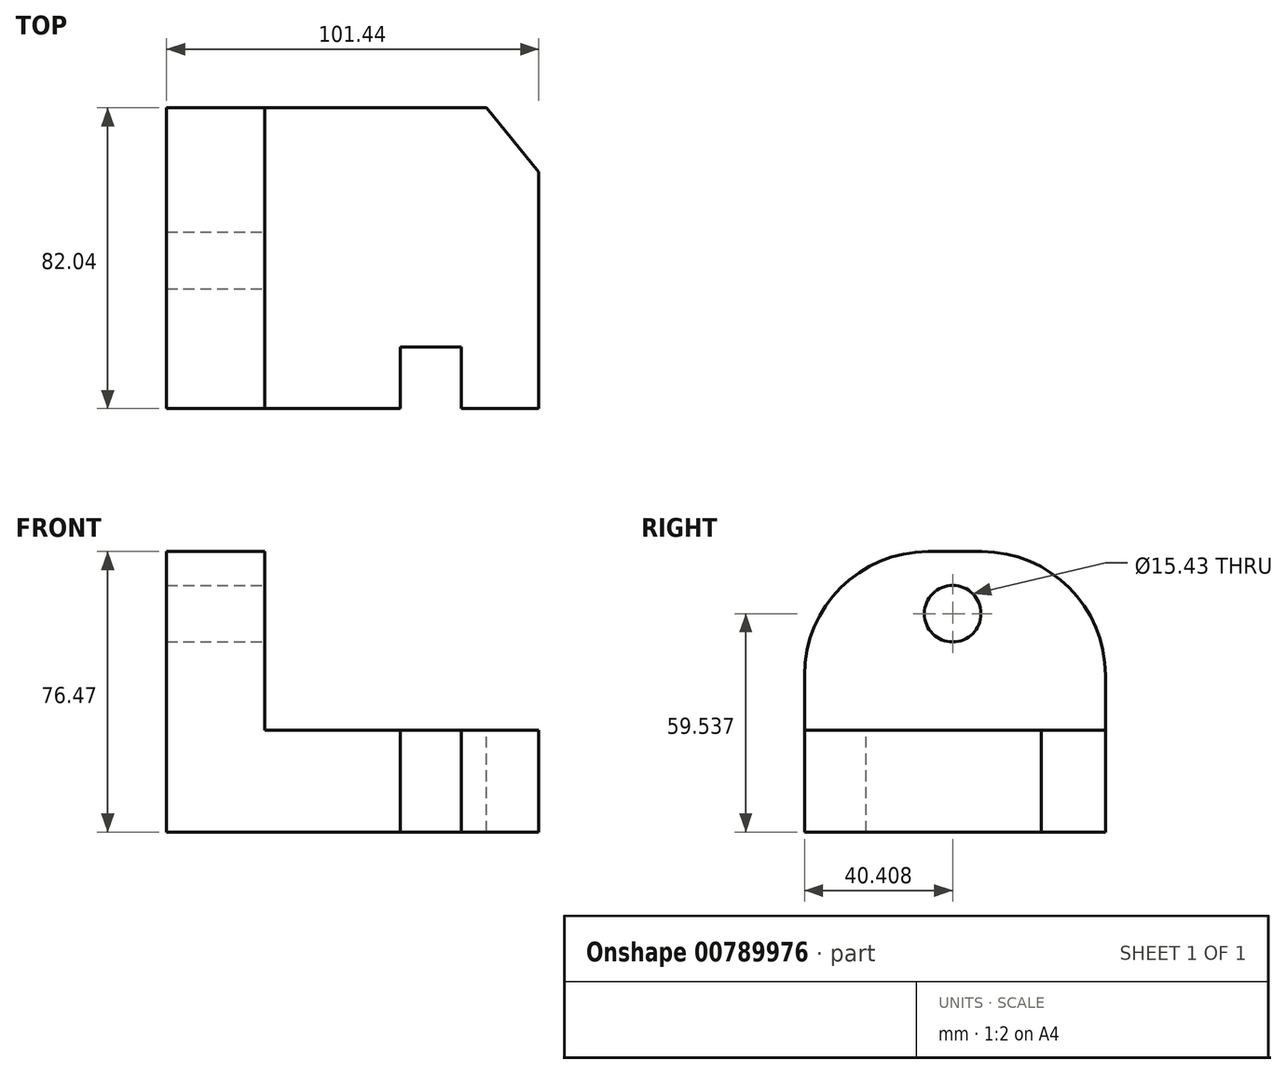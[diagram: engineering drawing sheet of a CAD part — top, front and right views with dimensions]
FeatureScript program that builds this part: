
annotation { "Feature Type Name" : "Feature", "Feature Type Description" : "" }
export const myFeature = defineFeature(function(context is Context, id is Id, definition is map)
    precondition{}
    {
        {
            var Q0;
            Q0=qCreatedBy(makeId("Front.planeOp"),FACE);
            var sketch = newSketch(context, id + "F0", { "sketchPlane" : qUnion([Q0])});
            skLineSegment(sketch, "E0", {"start": v(37.77, 0) * mm, "end": v(-36.84, 0) * mm});
            skLineSegment(sketch, "E1", {"start": v(-36.84, 0) * mm, "end": v(-36.84, 48.72) * mm});
            skLineSegment(sketch, "E2", {"start": v(-36.84, 48.72) * mm, "end": v(-63.67, 48.72) * mm});
            skLineSegment(sketch, "E3", {"start": v(-63.67, 48.72) * mm, "end": v(-63.67, -27.75) * mm});
            skLineSegment(sketch, "E4", {"start": v(-63.67, -27.75) * mm, "end": v(37.77, -27.75) * mm});
            skLineSegment(sketch, "E5", {"start": v(37.77, -27.75) * mm, "end": v(37.77, 0) * mm});
            skSolve(sketch);
        }
        {
            var Q0;
            Q0=makeQuery(id+"F0.imprint","IMPRINT",FACE,{"disambiguationData":[TD([[makeQuery(id+"F0.imprint","IMPRINT",EDGE,{"derivedFrom":sQuery(id+"F0.wireOp",EDGE,"E0")}),1.0]])]});
            extrude(context, id + "F1", {"entities" : qUnion([Q0]), "depth" : 82.04 * mm, "offsetDistance" : 25.4 * mm});
        }
        {
            var Q0;
            Q0=makeQuery(id+"F1.opExtrude","CAP_EDGE",EDGE,{"disambiguationData":[OSD([sQuery(id+"F0.wireOp",EDGE,"E2")])],"isStart":true});
            var Q1;
            Q1=makeQuery(id+"F1.opExtrude","CAP_EDGE",EDGE,{"disambiguationData":[OSD([sQuery(id+"F0.wireOp",EDGE,"E2")])],"isStart":false});
            fillet(context, id + "F2", {"entities" : qUnion([Q0, Q1]), "radius" : 33.73 * mm, "tangentPropagation" : true, "allowEdgeOverflow" : false});
        }
        {
            var Q0;
            Q0=makeQuery(id+"F1.opExtrude","SWEPT_FACE",FACE,{"disambiguationData":[OSD([sQuery(id+"F0.wireOp",EDGE,"E0")])]});
            var sketch = newSketch(context, id + "F3", { "sketchPlane" : qUnion([Q0])});
            skLineSegment(sketch, "E6", {"start": v(0, -82.04) * mm, "end": v(0, -65.2) * mm});
            skLineSegment(sketch, "E7", {"start": v(0, -65.2) * mm, "end": v(16.66, -65.2) * mm});
            skLineSegment(sketch, "E8", {"start": v(16.66, -65.2) * mm, "end": v(16.66, -82.04) * mm});
            skLineSegment(sketch, "E9", {"start": v(24.78, 0) * mm, "end": v(37.77, -14.32) * mm});
            skSolve(sketch);
        }
        {
            var Q0;
            {var subQ0=sQuery(id+"F3.wireOp",EDGE,"E6");Q0=makeQuery(id+"F3.imprint","IMPRINT",FACE,{"disambiguationData":[TD([[makeQuery(id+"F3.imprint","IMPRINT",EDGE,{"derivedFrom":subQ0}),-1.0]])]});}
            extrude(context, id + "F4", {"entities" : qUnion([Q0]), "operationType" : NewBodyOperationType.REMOVE, "endBound" : BoundingType.THROUGH_ALL, "oppositeDirection" : true, "depth" : 25.4 * mm, "offsetDistance" : 25.4 * mm});
        }
        {
            var Q0;
            Q0=makeQuery(id+"F1.opExtrude","SWEPT_FACE",FACE,{"disambiguationData":[OSD([sQuery(id+"F0.wireOp",EDGE,"E0")])]});
            var sketch = newSketch(context, id + "F5", { "sketchPlane" : qUnion([Q0])});
            skLineSegment(sketch, "E10", {"start": v(23.56, 0) * mm, "end": v(37.77, -17.5) * mm});
            skSolve(sketch);
        }
        {
            var Q0;
            {var subQ0=sQuery(id+"F5.wireOp",EDGE,"E10");Q0=makeQuery(id+"F5.imprint","IMPRINT",FACE,{"disambiguationData":[TD([[makeQuery(id+"F5.imprint","IMPRINT",EDGE,{"derivedFrom":subQ0}),1.0]])]});}
            extrude(context, id + "F6", {"entities" : qUnion([Q0]), "operationType" : NewBodyOperationType.REMOVE, "endBound" : BoundingType.THROUGH_ALL, "oppositeDirection" : true, "depth" : 25.4 * mm, "offsetDistance" : 25.4 * mm});
        }
        {
            var Q0;
            Q0=makeQuery(id+"F1.opExtrude","SWEPT_FACE",FACE,{"disambiguationData":[OSD([sQuery(id+"F0.wireOp",EDGE,"E1")])]});
            var sketch = newSketch(context, id + "F7", { "sketchPlane" : qUnion([Q0])});
            skCircle(sketch, "E11", {"center": v(-41.63, 31.79) * mm, "radius": 7.71 * mm});
            skSolve(sketch);
        }
        {
            var Q0;
            Q0=makeQuery(id+"F7.imprint","IMPRINT",FACE,{"disambiguationData":[TD([[makeQuery(id+"F7.imprint","IMPRINT",EDGE,{"derivedFrom":sQuery(id+"F7.wireOp",EDGE,"E11")}),1.0]])]});
            extrude(context, id + "F8", {"entities" : qUnion([Q0]), "operationType" : NewBodyOperationType.REMOVE, "endBound" : BoundingType.THROUGH_ALL, "oppositeDirection" : true, "depth" : 25.4 * mm, "offsetDistance" : 25.4 * mm});
        }
    });
